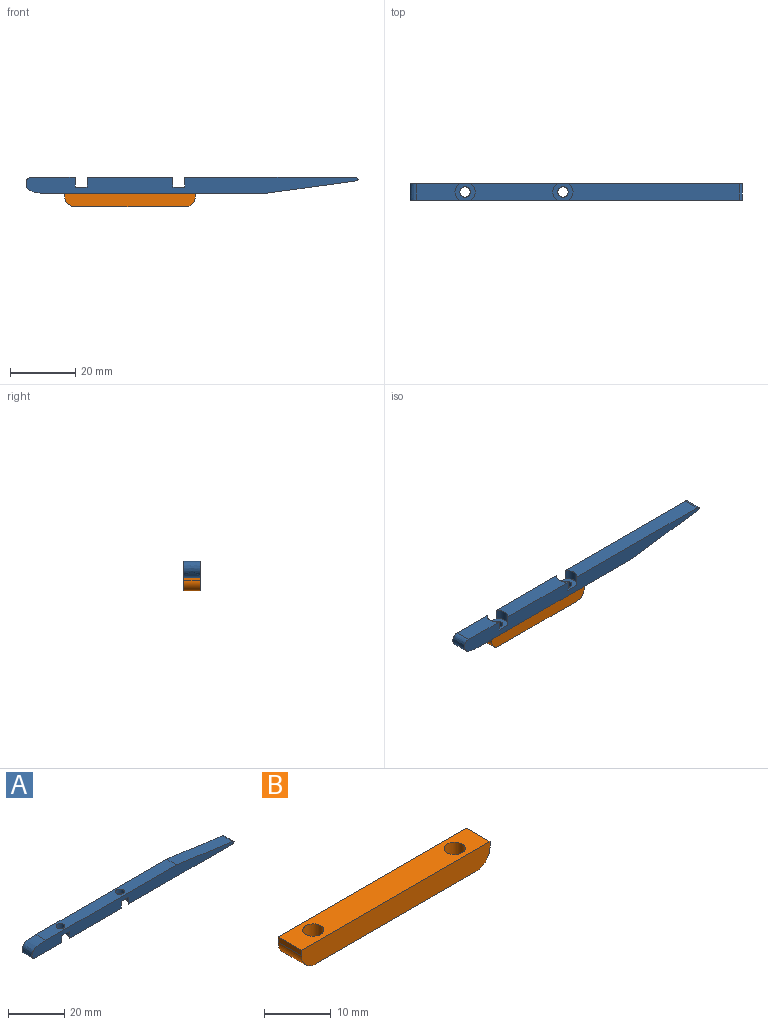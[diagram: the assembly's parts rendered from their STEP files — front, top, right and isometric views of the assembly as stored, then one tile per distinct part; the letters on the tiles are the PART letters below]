
ASSEMBLY  parts=2 mates=1
PART A: 18 faces, bbox 102x5x5 mm
  f0: plane 26.33x5mm, normal (0,0,-1), area 122.8mm2, adj f3,f9,f12,f15
  f1: plane 13.17x5mm, normal (0,0,-1), area 61.4mm2, adj f3,f6,f9,f13
  f2: plane 52.17x5mm, normal (0,0,-1), area 256.4mm2, adj f3,f9,f11,f16
  f3: plane 102.04x5mm, normal (0,-1,0), area 424.9mm2, adj f0,f1,f2,f6,f7,f8,f10,f11
  f4: cylinder r=1.6mm len=3.2mm, axis (0,0,-1), area 20.1mm2, adj f8,f17
  f5: cylinder r=1.6mm len=3.2mm, axis (0,0,-1), area 20.1mm2, adj f8,f14
  f6: extruded ~6.97x5mm, area 57.4mm2, adj f1,f3,f8,f9
  f7: plane 28.16x5mm, normal (0.14,0,0.99), area 142.1mm2, adj f3,f8,f9,f10
  f8: plane 65.9x5mm, normal (0,0,1), area 313.4mm2, adj f3,f4,f5,f6,f7,f9
  f9: plane 102.04x5mm, normal (0,1,0), area 424.9mm2, adj f0,f1,f2,f6,f7,f8,f10,f11
  f10: cylinder r=1mm len=5mm, axis (0,1,0), area 4.9mm2, adj f3,f7,f9,f11
  f11: cylinder r=1mm len=5mm, axis (0,1,0), area 5.6mm2, adj f2,f3,f9,f10
  f12: cylinder r=3.1mm len=5mm, axis (0,0,-1), area 17.4mm2, adj f0,f3,f9,f14
  f13: cylinder r=3.1mm len=5mm, axis (0,0,-1), area 17.4mm2, adj f1,f3,f9,f14
  f14: plane 6.2x5mm, normal (0,0,-1), area 19.2mm2, adj f3,f5,f9,f12,f13
  f15: cylinder r=3.1mm len=5mm, axis (0,0,-1), area 17.4mm2, adj f0,f3,f9,f17
  f16: cylinder r=3.1mm len=5mm, axis (0,0,-1), area 17.4mm2, adj f2,f3,f9,f17
  f17: plane 6.2x5mm, normal (0,0,-1), area 19.2mm2, adj f3,f4,f9,f15,f16
PART B: 10 faces, bbox 40x5x4 mm
  f0: plane 40x4mm, normal (0,-1,0), area 156.1mm2, adj f1,f3,f4,f5,f6,f7
  f1: plane 5x1mm, normal (1,0,0), area 5mm2, adj f0,f2,f4,f6
  f2: plane 40x4mm, normal (0,1,0), area 156.1mm2, adj f1,f3,f4,f5,f6,f7
  f3: plane 5x1mm, normal (-1,0,0), area 5mm2, adj f0,f2,f4,f7
  f4: plane 40x5mm, normal (0,0,1), area 183.9mm2, adj f0,f1,f2,f3,f8,f9
  f5: plane 34x5mm, normal (0,0,-1), area 153.9mm2, adj f0,f2,f6,f7,f8,f9
  f6: cylinder r=3mm len=5mm, axis (0,1,0), area 23.6mm2, adj f0,f1,f2,f5
  f7: cylinder r=3mm len=5mm, axis (0,-1,0), area 23.6mm2, adj f0,f2,f3,f5
  f8: cylinder r=1.6mm len=4mm, axis (0,0,-1), area 40.2mm2, adj f4,f5
  f9: cylinder r=1.6mm len=4mm, axis (0,0,-1), area 40.2mm2, adj f4,f5
PLACE A rot(axis=(1,0,0),180deg) t=(33.93,1.07,3.86)mm
PLACE B t=(-7.05,3.57,-5.14)mm
MATE fastened B.f8 <-> A.f4  axis (0,0,1) through (7.95,3.57,-1.14)mm
